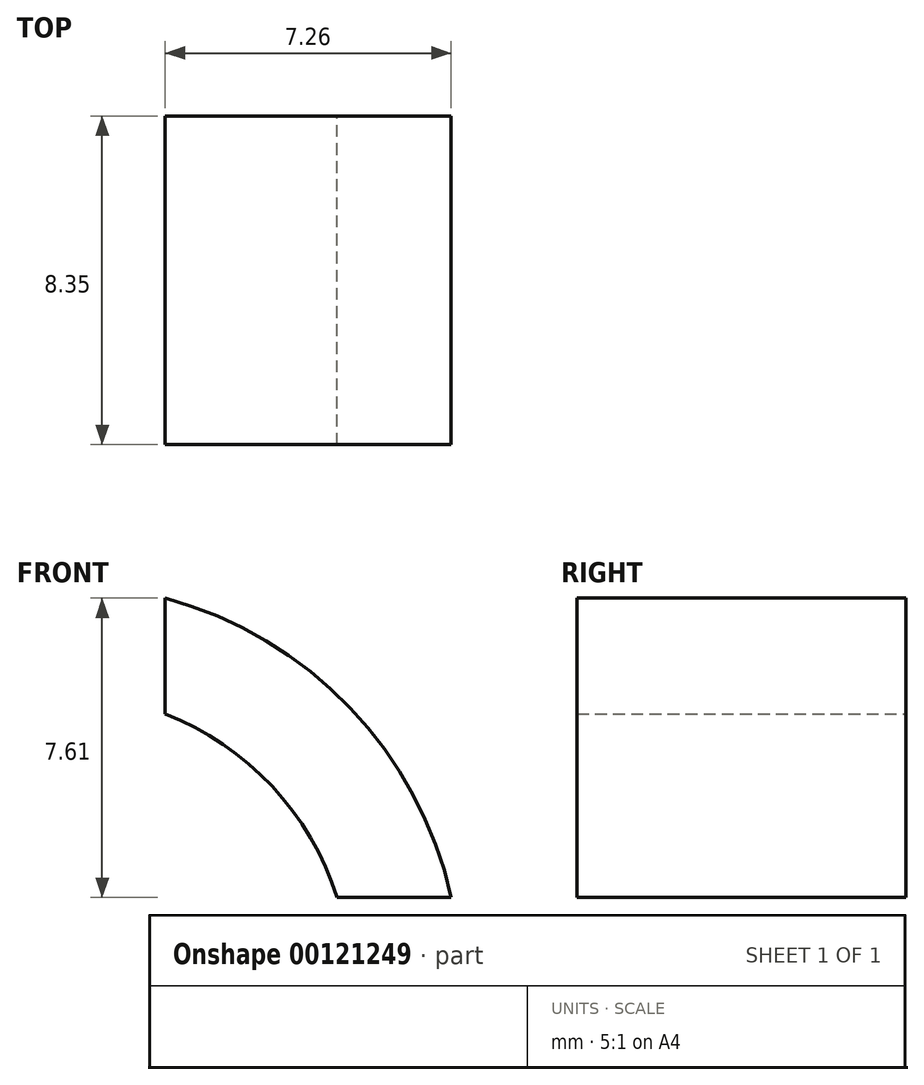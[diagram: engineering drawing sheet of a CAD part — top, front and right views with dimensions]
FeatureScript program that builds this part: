
annotation { "Feature Type Name" : "Feature", "Feature Type Description" : "" }
export const myFeature = defineFeature(function(context is Context, id is Id, definition is map)
    precondition{}
    {
        {
            var Q0;
            Q0=qCreatedBy(makeId("Front.planeOp"),FACE);
            var sketch = newSketch(context, id + "F0", { "sketchPlane" : qUnion([Q0])});
            skLineSegment(sketch, "E0", {"start": v(2.65, 6.86) * mm, "end": v(2.65, 9.8) * mm});
            skLineSegment(sketch, "E1", {"start": v(7.01, 2.2) * mm, "end": v(9.91, 2.2) * mm});
            skLineSegment(sketch, "E2", {"start": v(2.65, 9.8) * mm, "end": v(2.65, 9.8) * mm});
            skArc(sketch, "E3", {"start": v(7.01, 2.2) * mm, "mid": v(5.36, 5.03) * mm, "end": v(2.65, 6.86) * mm});
            skArc(sketch, "E4", {"start": v(9.91, 2.2) * mm, "mid": v(7.34, 7.02) * mm, "end": v(2.65, 9.8) * mm});
            skSolve(sketch);
        }
        {
            var Q0;
            Q0=qSketchRegion(id+"F0",true);
            extrude(context, id + "F1", {"entities" : qUnion([Q0]), "depth" : 8.35 * mm});
        }
    });
